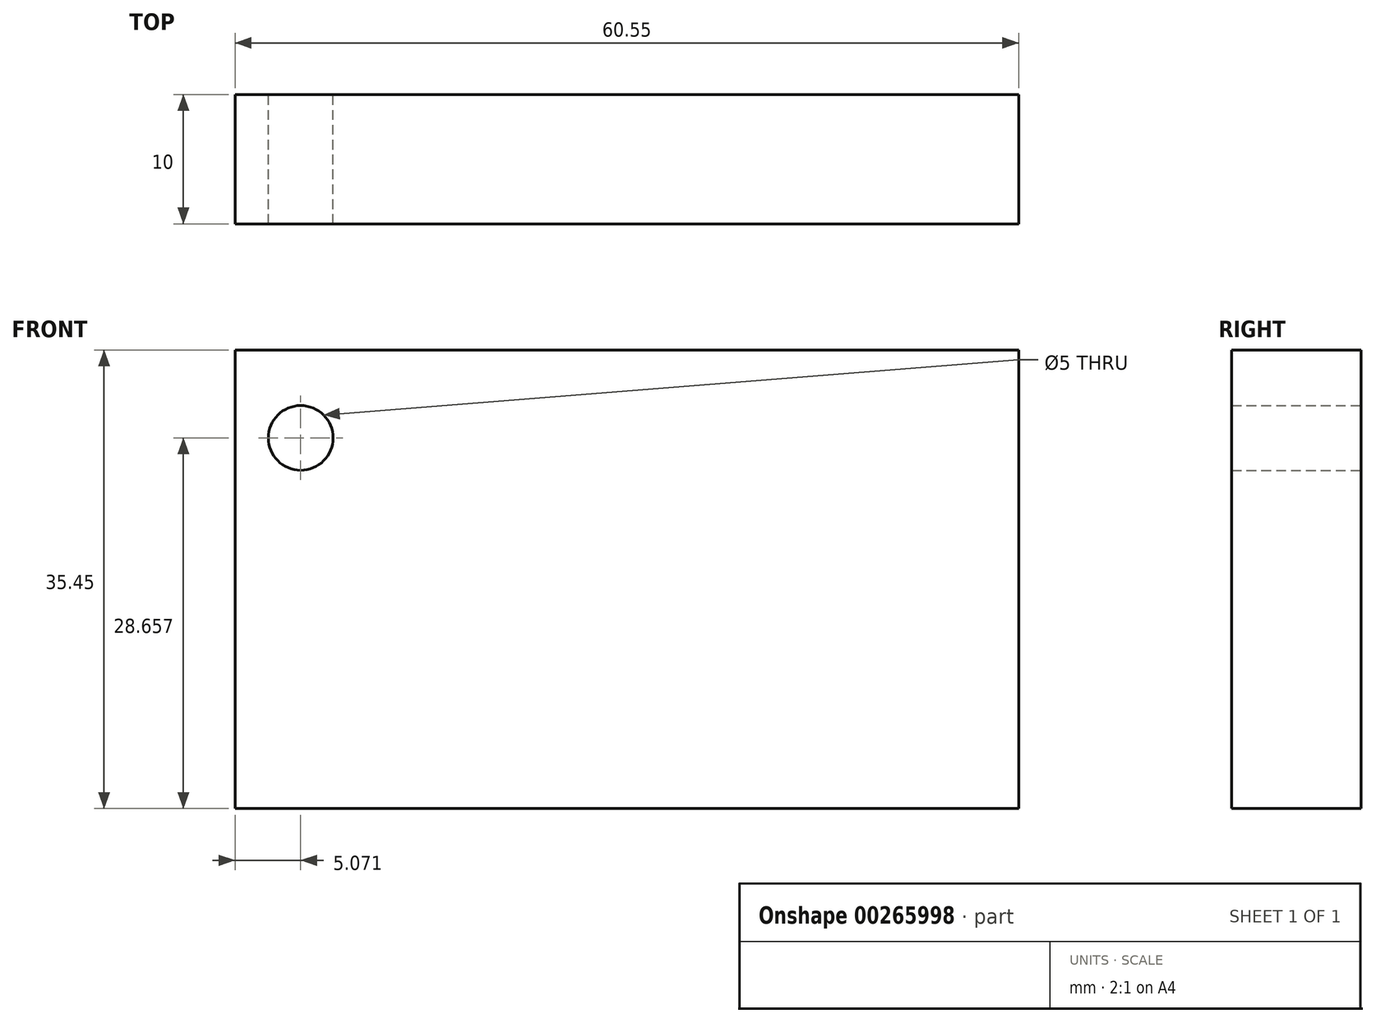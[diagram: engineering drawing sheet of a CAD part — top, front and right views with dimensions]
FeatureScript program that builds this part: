
annotation { "Feature Type Name" : "Feature", "Feature Type Description" : "" }
export const myFeature = defineFeature(function(context is Context, id is Id, definition is map)
    precondition{}
    {
        {
            var Q0;
            Q0=qCreatedBy(makeId("Front.planeOp"),FACE);
            var sketch = newSketch(context, id + "F0", { "sketchPlane" : qUnion([Q0])});
            skLineSegment(sketch, "E0.bottom", {"start": v(0, 0) * mm, "end": v(-60.55, 0) * mm});
            skLineSegment(sketch, "E0.top", {"start": v(0, 35.45) * mm, "end": v(-60.55, 35.45) * mm});
            skLineSegment(sketch, "E0.left", {"start": v(0, 0) * mm, "end": v(0, 35.45) * mm});
            skLineSegment(sketch, "E0.right", {"start": v(-60.55, 0) * mm, "end": v(-60.55, 35.45) * mm});
            skCircle(sketch, "E1", {"center": v(-55.48, 28.66) * mm, "radius": 2.5 * mm});
            skSolve(sketch);
        }
        {
            var Q0;
            Q0 = qSketchRegion(id + "F0", true);
            extrude(context, id + "F1", {"entities" : qUnion([Q0]), "depth" : 10 * mm});
        }
    });
